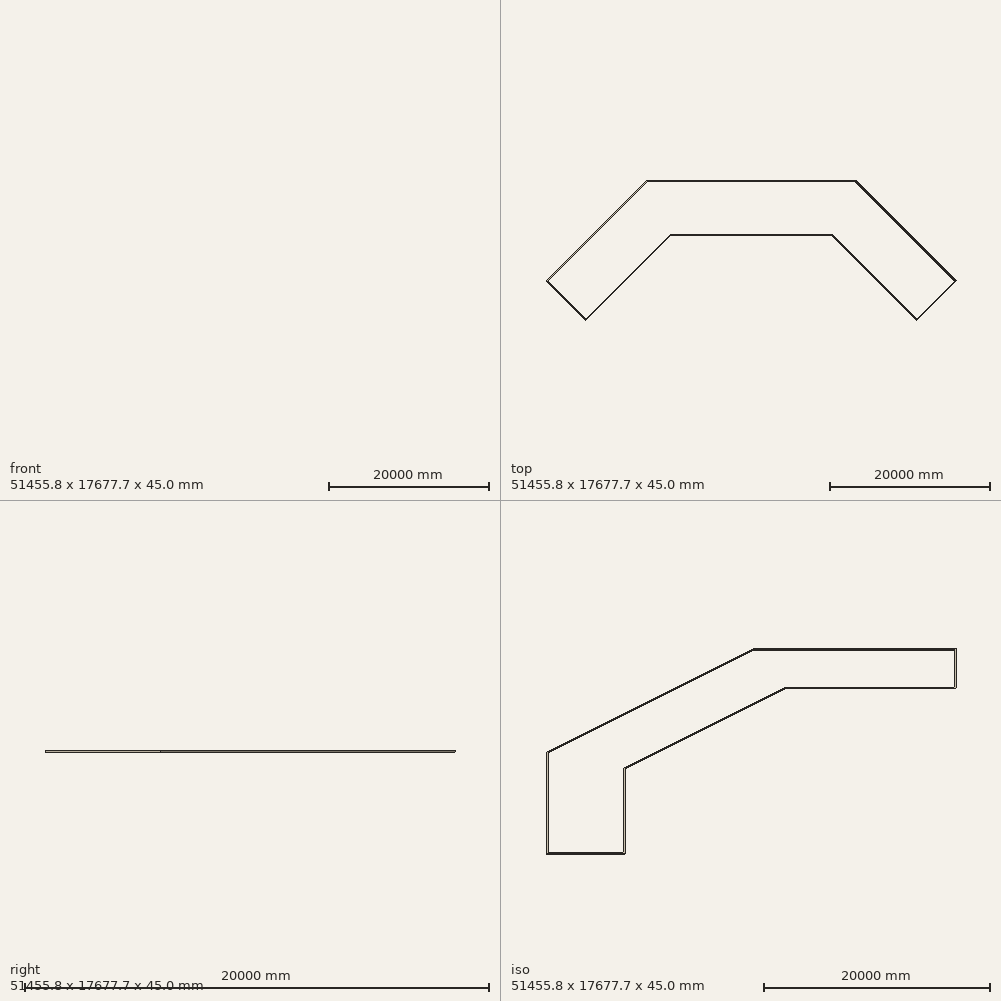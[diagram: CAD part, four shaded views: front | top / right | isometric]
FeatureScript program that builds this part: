
annotation { "Feature Type Name" : "Feature", "Feature Type Description" : "" }
export const myFeature = defineFeature(function(context is Context, id is Id, definition is map)
    precondition{}
    {
        {
            var Q0;
            Q0=qCreatedBy(makeId("Top.planeOp"),FACE);
            var sketch = newSketch(context, id + "F0", { "sketchPlane" : qUnion([Q0])});
            skLineSegment(sketch, "E0.bottom", {"start": v(13000, -3500) * mm, "end": v(10100.5, -3500) * mm, "construction": true});
            skLineSegment(sketch, "E0.top", {"start": v(13000, 3500) * mm, "end": v(-13000, 3500) * mm});
            skLineSegment(sketch, "E0.left", {"start": v(13000, -3500) * mm, "end": v(13000, 3500) * mm, "construction": true});
            skLineSegment(sketch, "E0.right", {"start": v(-13000, -3500) * mm, "end": v(-13000, 3500) * mm, "construction": true});
            skPoint(sketch, "E0.middle", {"position": v(0, 0) * mm});
            skLineSegment(sketch, "E1", {"start": v(13000, 3500) * mm, "end": v(25727.92, -9227.92) * mm});
            skLineSegment(sketch, "E2", {"start": v(25727.92, -9227.92) * mm, "end": v(20778.17, -14177.67) * mm});
            skLineSegment(sketch, "E3", {"start": v(20778.17, -14177.67) * mm, "end": v(10100.5, -3500) * mm});
            skLineSegment(sketch, "E4", {"start": v(13000, 3500) * mm, "end": v(10100.5, -3500) * mm, "construction": true});
            skLineSegment(sketch, "E5", {"start": v(-13000, 3500) * mm, "end": v(-25727.92, -9227.92) * mm});
            skLineSegment(sketch, "E6", {"start": v(-25727.92, -9227.92) * mm, "end": v(-20778.17, -14177.67) * mm});
            skLineSegment(sketch, "E7", {"start": v(-20778.17, -14177.67) * mm, "end": v(-10100.5, -3500) * mm});
            skLineSegment(sketch, "E8", {"start": v(-13000, 3500) * mm, "end": v(-10100.5, -3500) * mm, "construction": true});
            skLineSegment(sketch, "E9", {"start": v(-10100.5, -3500) * mm, "end": v(-13000, -3500) * mm, "construction": true});
            skLineSegment(sketch, "E10", {"start": v(10100.5, -3500) * mm, "end": v(-10100.5, -3500) * mm});
            skLineSegment(sketch, "E11.0", {"start": v(12939.94, 3355) * mm, "end": v(-12939.94, 3355) * mm});
            skLineSegment(sketch, "E11.1", {"start": v(12939.94, 3355) * mm, "end": v(25522.86, -9227.92) * mm});
            skLineSegment(sketch, "E11.2", {"start": v(-12939.94, 3355) * mm, "end": v(-25522.86, -9227.92) * mm});
            skLineSegment(sketch, "E11.3", {"start": v(25522.86, -9227.92) * mm, "end": v(20778.17, -13972.6) * mm});
            skLineSegment(sketch, "E11.4", {"start": v(-25522.86, -9227.92) * mm, "end": v(-20778.17, -13972.6) * mm});
            skLineSegment(sketch, "E11.5", {"start": v(-20778.17, -13972.6) * mm, "end": v(-10160.57, -3355) * mm});
            skLineSegment(sketch, "E11.6", {"start": v(10160.57, -3355) * mm, "end": v(-10160.57, -3355) * mm});
            skLineSegment(sketch, "E11.7", {"start": v(20778.17, -13972.6) * mm, "end": v(10160.57, -3355) * mm});
            skSolve(sketch);
        }
        {
            var Q0;
            Q0=makeQuery(id+"F0.imprint","IMPRINT",FACE,{"disambiguationData":[TD([[makeQuery(id+"F0.imprint","IMPRINT",EDGE,{"derivedFrom":sQuery(id+"F0.wireOp",EDGE,"E0.top")}),1.0]])]});
            extrude(context, id + "F1", {"entities" : qUnion([Q0]), "depth" : 45 * mm, "offsetDistance" : 25 * mm});
        }
        {
            var Q0;
            Q0=qCreatedBy(makeId("Top.planeOp"),FACE);
            var sketch = newSketch(context, id + "F2", { "sketchPlane" : qUnion([Q0])});
            skLineSegment(sketch, "E12.0", {"start": v(13000, 3500) * mm, "end": v(-13000, 3500) * mm});
            skLineSegment(sketch, "E13.0", {"start": v(13000, 3500) * mm, "end": v(25727.92, -9227.92) * mm});
            skLineSegment(sketch, "E14.0", {"start": v(25727.92, -9227.92) * mm, "end": v(20778.17, -14177.67) * mm});
            skLineSegment(sketch, "E15.0", {"start": v(20778.17, -14177.67) * mm, "end": v(10100.5, -3500) * mm});
            skLineSegment(sketch, "E16.0", {"start": v(10100.5, -3500) * mm, "end": v(-10100.5, -3500) * mm});
            skLineSegment(sketch, "E17.0", {"start": v(-20778.17, -14177.67) * mm, "end": v(-10100.5, -3500) * mm});
            skLineSegment(sketch, "E18.0", {"start": v(-25727.92, -9227.92) * mm, "end": v(-20778.17, -14177.67) * mm});
            skLineSegment(sketch, "E19.0", {"start": v(-13000, 3500) * mm, "end": v(-25727.92, -9227.92) * mm});
            skLineSegment(sketch, "E20", {"start": v(11550.25, 0) * mm, "end": v(-11550.25, 0) * mm, "construction": true});
            skLineSegment(sketch, "E21", {"start": v(-23253.05, -11702.8) * mm, "end": v(-11550.25, 0) * mm, "construction": true});
            skLineSegment(sketch, "E22", {"start": v(23253.05, -11702.8) * mm, "end": v(11550.25, 0) * mm, "construction": true});
            skLineSegment(sketch, "E23", {"start": v(13000, 3500) * mm, "end": v(10100.5, -3500) * mm, "construction": true});
            skLineSegment(sketch, "E24", {"start": v(-13000, 3500) * mm, "end": v(-10100.5, -3500) * mm, "construction": true});
            skLineSegment(sketch, "E25", {"start": v(0, -3500) * mm, "end": v(0, 3500) * mm, "construction": true});
            skLineSegment(sketch, "E26", {"start": v(-16535.53, -9935.03) * mm, "end": v(-21485.28, -4985.28) * mm, "construction": true});
            skLineSegment(sketch, "E27", {"start": v(-12292.9, -5692.39) * mm, "end": v(-17242.64, -742.64) * mm, "construction": true});
            skLineSegment(sketch, "E28", {"start": v(-6500, 3500) * mm, "end": v(-6500, -3500) * mm, "construction": true});
            skLineSegment(sketch, "E29.MirrorCS", {"start": v(6500, 3500) * mm, "end": v(6500, -3500) * mm, "construction": true});
            skLineSegment(sketch, "E30.MirrorCS", {"start": v(12292.9, -5692.39) * mm, "end": v(17242.64, -742.64) * mm, "construction": true});
            skLineSegment(sketch, "E31.MirrorCS", {"start": v(16535.53, -9935.03) * mm, "end": v(21485.28, -4985.28) * mm, "construction": true});
            skSolve(sketch);
        }
        {
            var Q0;
            Q0=sQuery(id+"F2.wireOp",EDGE,"E25");
            cPlane(context, id + "F3", {"entities" : qUnion([Q0]), "cplaneType" : CPlaneType.LINE_ANGLE, "offset" : 25 * mm, "angle" : 90 * degree, "width" : 150 * mm, "height" : 150 * mm});
        }
    });
